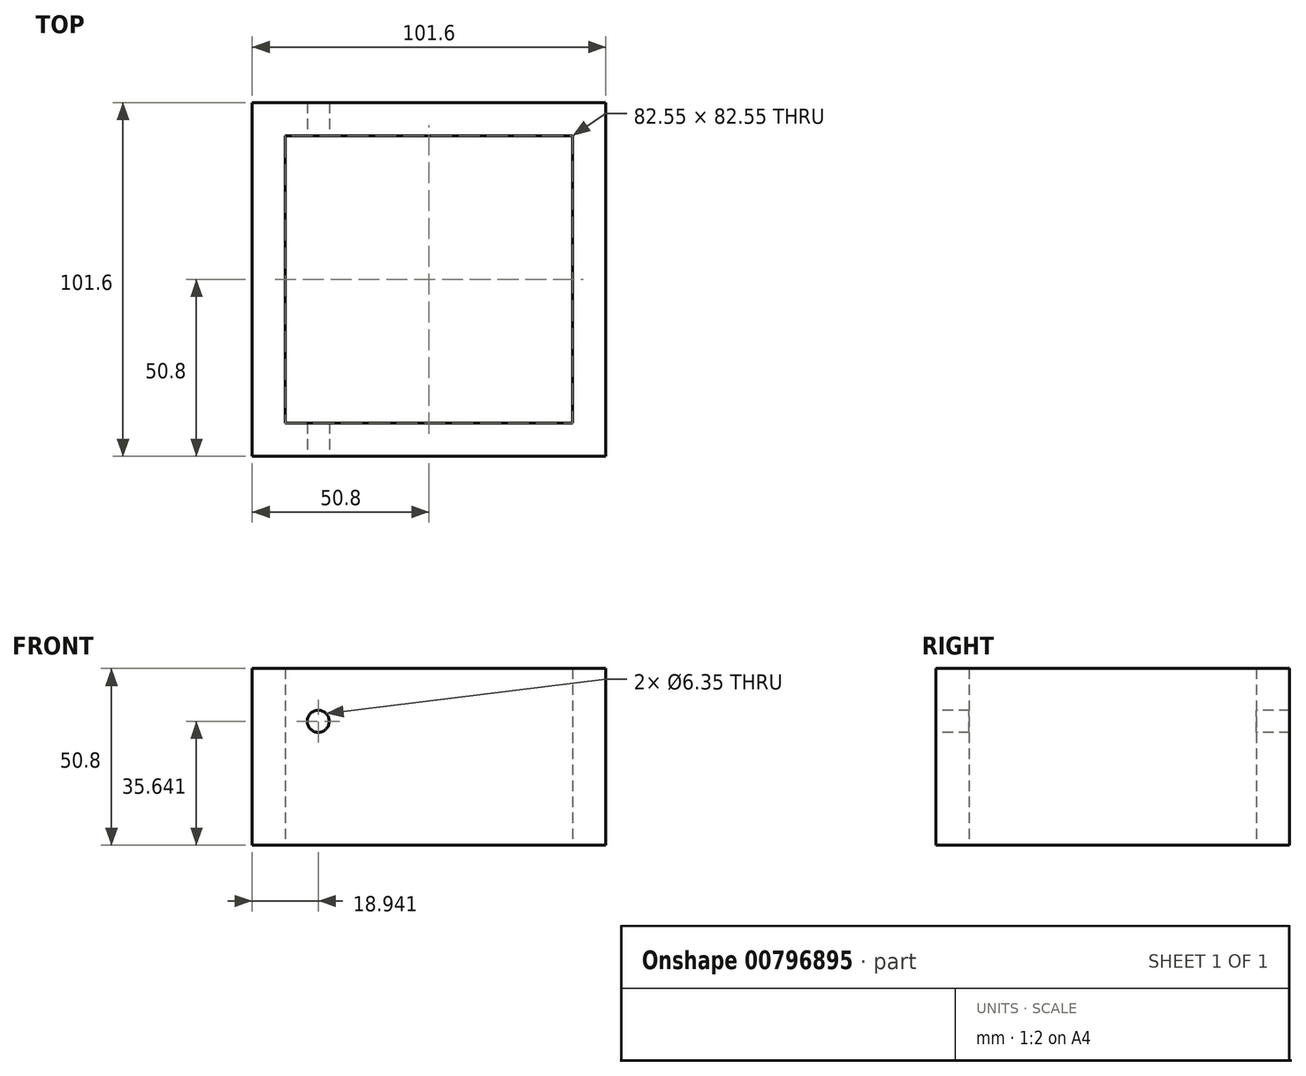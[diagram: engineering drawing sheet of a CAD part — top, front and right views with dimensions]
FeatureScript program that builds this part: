
annotation { "Feature Type Name" : "Feature", "Feature Type Description" : "" }
export const myFeature = defineFeature(function(context is Context, id is Id, definition is map)
    precondition{}
    {
        {
            var Q0;
            Q0=qCreatedBy(makeId("Top.planeOp"),FACE);
            var sketch = newSketch(context, id + "F0", { "sketchPlane" : qUnion([Q0])});
            skLineSegment(sketch, "E0.bottom", {"start": v(-50.8, 50.8) * mm, "end": v(50.8, 50.8) * mm});
            skLineSegment(sketch, "E0.top", {"start": v(-50.8, -50.8) * mm, "end": v(50.8, -50.8) * mm});
            skLineSegment(sketch, "E0.left", {"start": v(-50.8, 50.8) * mm, "end": v(-50.8, -50.8) * mm});
            skLineSegment(sketch, "E0.right", {"start": v(50.8, 50.8) * mm, "end": v(50.8, -50.8) * mm});
            skLineSegment(sketch, "E1.bottom", {"start": v(41.27, 41.28) * mm, "end": v(-41.27, 41.28) * mm});
            skLineSegment(sketch, "E1.top", {"start": v(41.27, -41.27) * mm, "end": v(-41.27, -41.27) * mm});
            skLineSegment(sketch, "E1.left", {"start": v(41.27, 41.27) * mm, "end": v(41.27, -41.28) * mm});
            skLineSegment(sketch, "E1.right", {"start": v(-41.27, 41.27) * mm, "end": v(-41.27, -41.28) * mm});
            skPoint(sketch, "E1.middle", {"position": v(0, 0) * mm});
            skSolve(sketch);
        }
        {
            var Q0;
            Q0=makeQuery(id+"F0.imprint","IMPRINT",FACE,{"disambiguationData":[TD([[makeQuery(id+"F0.imprint","IMPRINT",EDGE,{"derivedFrom":sQuery(id+"F0.wireOp",EDGE,"E0.bottom")}),-1.0]])]});
            extrude(context, id + "F1", {"entities" : qUnion([Q0]), "depth" : 50.8 * mm, "offsetDistance" : 25.4 * mm});
        }
        {
            var Q0;
            Q0=makeQuery(id+"F1.opExtrude","SWEPT_FACE",FACE,{"disambiguationData":[OSD([sQuery(id+"F0.wireOp",EDGE,"E0.top")])]});
            var sketch = newSketch(context, id + "F2", { "sketchPlane" : qUnion([Q0])});
            skCircle(sketch, "E2", {"center": v(-31.86, 35.64) * mm, "radius": 3.18 * mm});
            skSolve(sketch);
        }
        {
            var Q0;
            Q0 = qSketchRegion(id + "F2", true);
            extrude(context, id + "F3", {"entities" : qUnion([Q0]), "operationType" : NewBodyOperationType.REMOVE, "oppositeDirection" : true, "depth" : 150.62 * mm, "offsetDistance" : 25.4 * mm});
        }
    });
